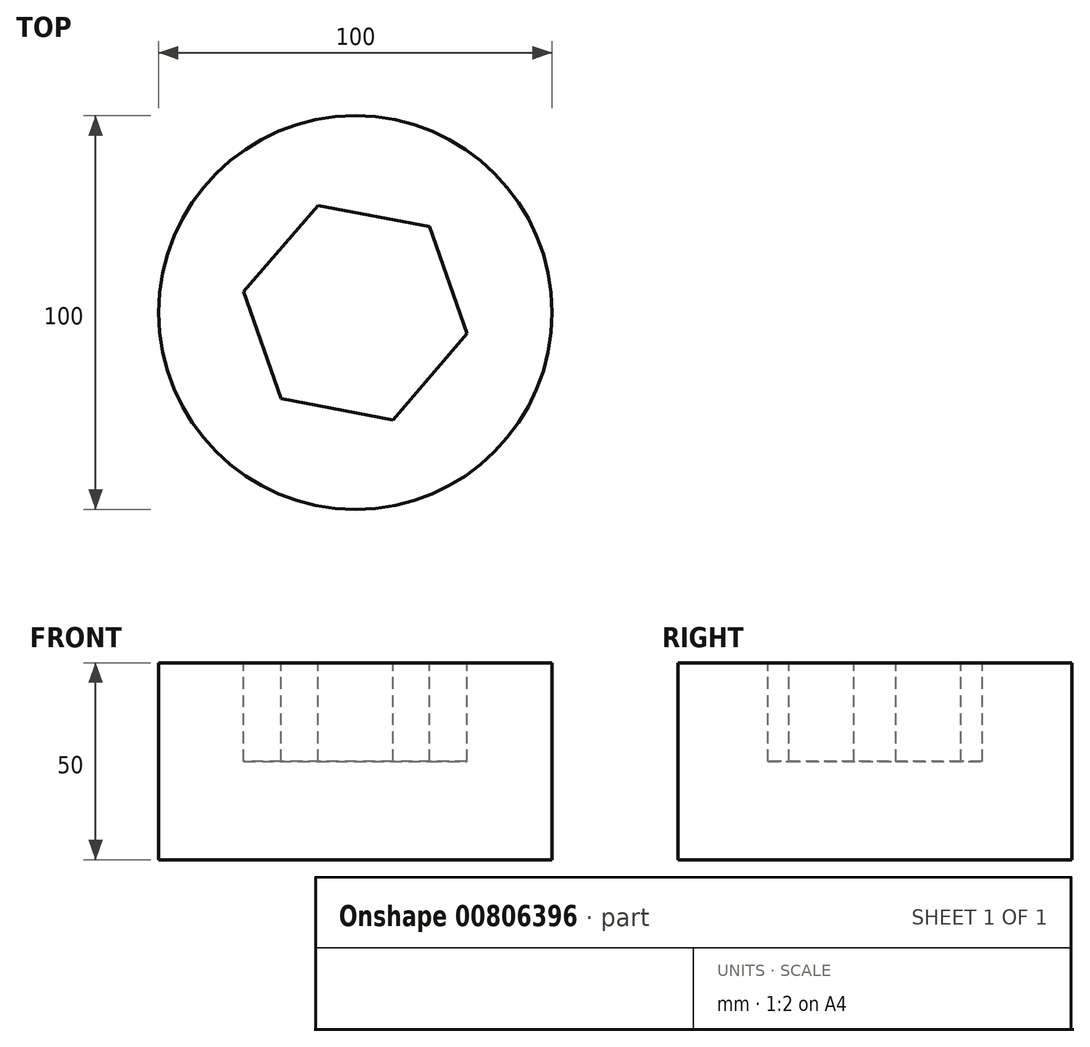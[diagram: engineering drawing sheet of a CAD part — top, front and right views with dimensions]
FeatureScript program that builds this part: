
annotation { "Feature Type Name" : "Feature", "Feature Type Description" : "" }
export const myFeature = defineFeature(function(context is Context, id is Id, definition is map)
    precondition{}
    {
        {
            var Q0;
            Q0=qCreatedBy(makeId("Top.planeOp"),FACE);
            var sketch = newSketch(context, id + "F0", { "sketchPlane" : qUnion([Q0])});
            skCircle(sketch, "E0", {"center": v(0, -4.99) * mm, "radius": 50 * mm});
            skSolve(sketch);
        }
        {
            var Q0;
            Q0=makeQuery(id+"F0.imprint","IMPRINT",FACE,{"disambiguationData":[TD([[makeQuery(id+"F0.imprint","IMPRINT",EDGE,{"derivedFrom":sQuery(id+"F0.wireOp",EDGE,"E0")}),1.0]])]});
            extrude(context, id + "F1", {"entities" : qUnion([Q0]), "depth" : 50 * mm, "offsetDistance" : 25 * mm});
        }
        {
            var Q0;
            Q0=makeQuery(id+"F1.opExtrude","CAP_FACE",FACE,{"disambiguationData":[OSD([sQuery(id+"F0.wireOp",EDGE,"E0")])],"isStart":false});
            var sketch = newSketch(context, id + "F2", { "sketchPlane" : qUnion([Q0])});
            skCircle(sketch, "E1.cCircle", {"center": v(0, -4.99) * mm, "radius": 25 * mm, "construction": true});
            skLineSegment(sketch, "E1.0", {"start": v(-28.36, 0.38) * mm, "end": v(-9.53, 22.26) * mm});
            skLineSegment(sketch, "E1.1", {"start": v(-9.53, 22.26) * mm, "end": v(18.83, 16.9) * mm});
            skLineSegment(sketch, "E1.2", {"start": v(18.83, 16.9) * mm, "end": v(28.36, -10.36) * mm});
            skLineSegment(sketch, "E1.3", {"start": v(28.36, -10.36) * mm, "end": v(9.53, -32.23) * mm});
            skLineSegment(sketch, "E1.4", {"start": v(9.53, -32.23) * mm, "end": v(-18.83, -26.86) * mm});
            skLineSegment(sketch, "E1.5", {"start": v(-18.83, -26.86) * mm, "end": v(-28.36, 0.38) * mm});
            skPoint(sketch, "E1.0.midPoint", {"position": v(-18.95, 11.32) * mm});
            skSolve(sketch);
        }
        {
            var Q0;
            Q0 = qSketchRegion(id + "F2", true);
            extrude(context, id + "F3", {"entities" : qUnion([Q0]), "operationType" : NewBodyOperationType.REMOVE, "oppositeDirection" : true, "depth" : 25 * mm, "offsetDistance" : 25 * mm});
        }
    });
